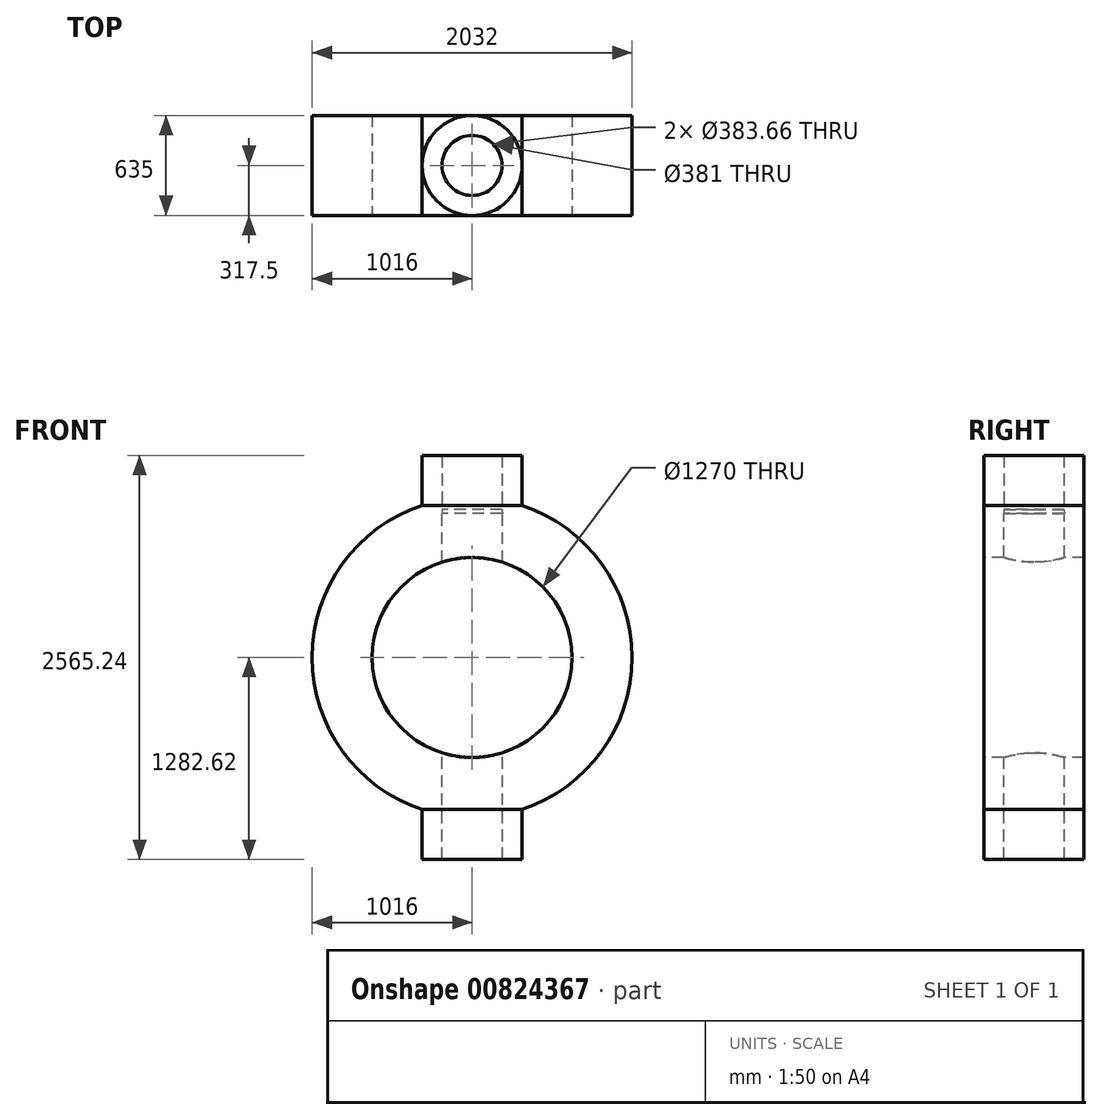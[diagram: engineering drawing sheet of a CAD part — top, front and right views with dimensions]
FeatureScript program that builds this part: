
annotation { "Feature Type Name" : "Feature", "Feature Type Description" : "" }
export const myFeature = defineFeature(function(context is Context, id is Id, definition is map)
    precondition{}
    {
        {
            var Q0;
            Q0=qCreatedBy(makeId("Front.planeOp"),FACE);
            var sketch = newSketch(context, id + "F0", { "sketchPlane" : qUnion([Q0])});
            skCircle(sketch, "E0", {"center": v(0, 0) * mm, "radius": 635 * mm});
            skArc(sketch, "E1", {"start": v(-317.5, 965.12) * mm, "mid": v(-1016, 0) * mm, "end": v(-317.5, -965.12) * mm});
            skLineSegment(sketch, "E2", {"start": v(-317.5, 965.12) * mm, "end": v(317.5, 965.12) * mm});
            skLineSegment(sketch, "E3", {"start": v(-317.5, -965.12) * mm, "end": v(317.5, -965.12) * mm});
            skArc(sketch, "E4.trimOffspring", {"start": v(317.5, -965.12) * mm, "mid": v(1016, 0) * mm, "end": v(317.5, 965.12) * mm});
            skSolve(sketch);
        }
        {
            var Q0;
            Q0=makeQuery(id+"F0.imprint","IMPRINT",FACE,{"disambiguationData":[TD([[makeQuery(id+"F0.imprint","IMPRINT",EDGE,{"derivedFrom":sQuery(id+"F0.wireOp",EDGE,"E0")}),-1.0]])]});
            var Q1;
            Q1=makeQuery(id+"F0.imprint","IMPRINT",FACE,{"disambiguationData":[TD([[makeQuery(id+"F0.imprint","IMPRINT",EDGE,{"derivedFrom":sQuery(id+"F0.wireOp",EDGE,"E0")}),1.0]])]});
            extrude(context, id + "F1", {"entities" : qUnion([Q0, Q1]), "depth" : 635 * mm, "offsetDistance" : 25.4 * mm});
        }
        {
            var Q0;
            Q0=makeQuery(id+"F1.opExtrude","SWEPT_FACE",FACE,{"disambiguationData":[OSD([sQuery(id+"F0.wireOp",EDGE,"E2")])]});
            var sketch = newSketch(context, id + "F2", { "sketchPlane" : qUnion([Q0])});
            skCircle(sketch, "E5", {"center": v(0, -317.5) * mm, "radius": 317.5 * mm});
            skPoint(sketch, "E5.centerSnap0", {"position": v(-317.5, -317.5) * mm});
            skCircle(sketch, "E6", {"center": v(0, -317.5) * mm, "radius": 190.5 * mm});
            skSolve(sketch);
        }
        {
            var Q0;
            Q0=makeQuery(id+"F2.imprint","IMPRINT",FACE,{"disambiguationData":[TD([[makeQuery(id+"F2.imprint","IMPRINT",EDGE,{"derivedFrom":sQuery(id+"F2.wireOp",EDGE,"E6")}),-1.0]])]});
            extrude(context, id + "F3", {"entities" : qUnion([Q0]), "operationType" : NewBodyOperationType.ADD, "depth" : 317.5 * mm, "offsetDistance" : 25.4 * mm});
        }
        {
            var Q0;
            Q0=makeQuery(id+"F3.boolean.opBoolean","SPLIT",FACE,{"disambiguationData":[TD([makeQuery(id+"F3.opExtrude","SWEPT_FACE",FACE,{"disambiguationData":[OSD([sQuery(id+"F2.wireOp",EDGE,"E6")])]})])],"derivedFrom":makeQuery(id+"F1.opExtrude","SWEPT_FACE",FACE,{"disambiguationData":[OSD([sQuery(id+"F0.wireOp",EDGE,"E2")])]})});
            extrude(context, id + "F4", {"entities" : qUnion([Q0]), "operationType" : NewBodyOperationType.REMOVE, "oppositeDirection" : true, "depth" : 25.4 * mm, "offsetDistance" : 25.4 * mm});
        }
        {
            var Q0;
            Q0=makeQuery(id+"F4.boolean.opBoolean","COPY",FACE,{"derivedFrom":makeQuery(id+"F4.opExtrude","CAP_FACE",FACE,{"disambiguationData":[OSD([sQuery(id+"F0.wireOp",EDGE,"E2")])],"isStart":false})});
            extrude(context, id + "F5", {"entities" : qUnion([Q0]), "operationType" : NewBodyOperationType.REMOVE, "oppositeDirection" : true, "depth" : 25.4 * mm, "offsetDistance" : 25.4 * mm, "hasDraft" : true, "draftAngle" : 3 * degree});
        }
        {
            var Q0;
            Q0=makeQuery(id+"F5.boolean.opBoolean","COPY",FACE,{"derivedFrom":makeQuery(id+"F5.opExtrude","CAP_FACE",FACE,{"disambiguationData":[OSD([sQuery(id+"F0.wireOp",EDGE,"E2")])],"isStart":false})});
            extrude(context, id + "F6", {"entities" : qUnion([Q0]), "operationType" : NewBodyOperationType.REMOVE, "endBound" : BoundingType.THROUGH_ALL, "oppositeDirection" : true, "depth" : 25.4 * mm, "offsetDistance" : 25.4 * mm});
        }
        {
            var Q0;
            Q0=makeQuery(id+"F1.opExtrude","SWEPT_FACE",FACE,{"disambiguationData":[OSD([sQuery(id+"F0.wireOp",EDGE,"E3")])]});
            var sketch = newSketch(context, id + "F7", { "sketchPlane" : qUnion([Q0])});
            skSolve(sketch);
        }
        {
            var Q0;
            {var subQ0=sQuery(id+"F0.wireOp",EDGE,"E3");Q0=makeQuery(id+"F7.imprint","IMPRINT",FACE,{"disambiguationData":[TD([[makeQuery(id+"F7.imprint","IMPRINT",EDGE,{"derivedFrom":makeQuery(id+"F1.opExtrude","CAP_EDGE",EDGE,{"disambiguationData":[OSD([subQ0])],"isStart":true})}),1.0]])]});}
            var sketch = newSketch(context, id + "F8", { "sketchPlane" : qUnion([Q0])});
            skCircle(sketch, "E7", {"center": v(0, 317.5) * mm, "radius": 317.5 * mm});
            skSolve(sketch);
        }
        {
            var Q0;
            {var subQ1=sQuery(id+"F0.wireOp",EDGE,"E3");Q0=makeQuery(id+"F8.imprint","IMPRINT",FACE,{"disambiguationData":[TD([[makeQuery(id+"F8.imprint","IMPRINT",EDGE,{"derivedFrom":makeQuery(id+"F7.imprint","IMPRINT",EDGE,{"derivedFrom":makeQuery(id+"F6.boolean.opBoolean","INTERSECT",EDGE,{"derivedFrom":[makeQuery(id+"F1.opExtrude","SWEPT_FACE",FACE,{"disambiguationData":[OSD([subQ1])]}),makeQuery(id+"F6.opExtrude","SWEPT_FACE",FACE,{"disambiguationData":[OSD([sQuery(id+"F2.wireOp",EDGE,"E6")])]})]})})}),1.0]])]});}
            extrude(context, id + "F9", {"entities" : qUnion([Q0]), "operationType" : NewBodyOperationType.ADD, "depth" : 317.5 * mm, "offsetDistance" : 25.4 * mm});
        }
        {
            var Q0;
            Q0=makeQuery(id+"F1.opExtrude","CAP_FACE",FACE,{"disambiguationData":[OSD([sQuery(id+"F0.wireOp",EDGE,"E1"),sQuery(id+"F0.wireOp",EDGE,"E2"),sQuery(id+"F0.wireOp",EDGE,"E3"),sQuery(id+"F0.wireOp",EDGE,"E4.trimOffspring")])],"isStart":false});
            var sketch = newSketch(context, id + "F10", { "sketchPlane" : qUnion([Q0])});
            skCircle(sketch, "E8", {"center": v(0, 0) * mm, "radius": 635 * mm});
            skSolve(sketch);
        }
        {
            var Q0;
            Q0=makeQuery(id+"F10.imprint","IMPRINT",FACE,{"disambiguationData":[TD([[makeQuery(id+"F10.imprint","IMPRINT",EDGE,{"derivedFrom":sQuery(id+"F10.wireOp",EDGE,"E8")}),1.0]])]});
            extrude(context, id + "F11", {"entities" : qUnion([Q0]), "operationType" : NewBodyOperationType.REMOVE, "endBound" : BoundingType.THROUGH_ALL, "oppositeDirection" : true, "depth" : 25.4 * mm, "offsetDistance" : 25.4 * mm});
        }
    });
